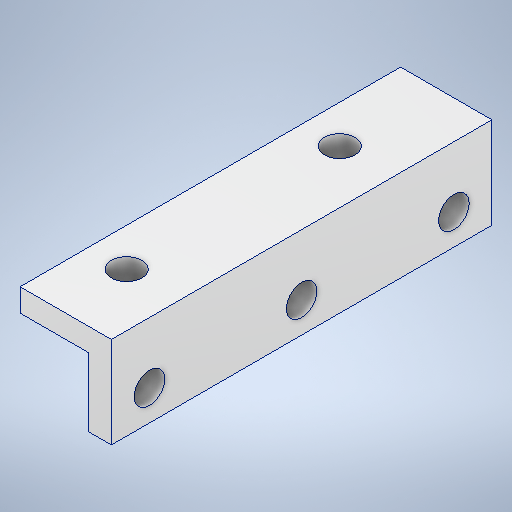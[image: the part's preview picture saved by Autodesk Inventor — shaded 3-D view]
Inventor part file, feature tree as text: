
AUTODESK INVENTOR PART (.ipt)
format: ipt  version: 2025.1 (Build 291241000, 241)  size: 254,464 bytes
history: native  units: mm
features: sketch x3, hole x2, extrude x1
ambient origin geometry x8: Origin, YZ Plane, XZ Plane, XY Plane, X Axis, Y Axis, Z Axis, Center Point
bodies: Volumenkörper1 (feature_tree)
feature tree (6):
  extrude  "Extrusion1"  Depth=3.0mm
  hole  "Bohrung1"  [1 undecoded]
  hole  "Bohrung2"  [1 undecoded]
  sketch  "Skizze1"  dims[d0=12.0mm d1=3.0mm]
  sketch  "Skizze2"  dims[d2=12.0mm d3=3.0mm]
  sketch  "Skizze3"  dims[d4=50.0mm d5=0.0mm d6=4.0mm d7=6.0mm d8=4.0mm d9=2.0mm d10=90.0deg d11=8.0mm d12=20.594885mm d13=4.0mm d16=4.0mm d17=6.0mm d18=4.0mm d19=2.0mm d20=90.0deg d21=8.0mm d22=20.594885mm d26=28.0mm d28=5.0mm d29=5.0mm d30=5.0mm d31=20.0mm d32=9.0mm]
note: 2 required parameter values undecoded (feature->parameter linkage not recoverable at this tier; creation-order binding heuristic only, values carry confidence <= 0.55)
